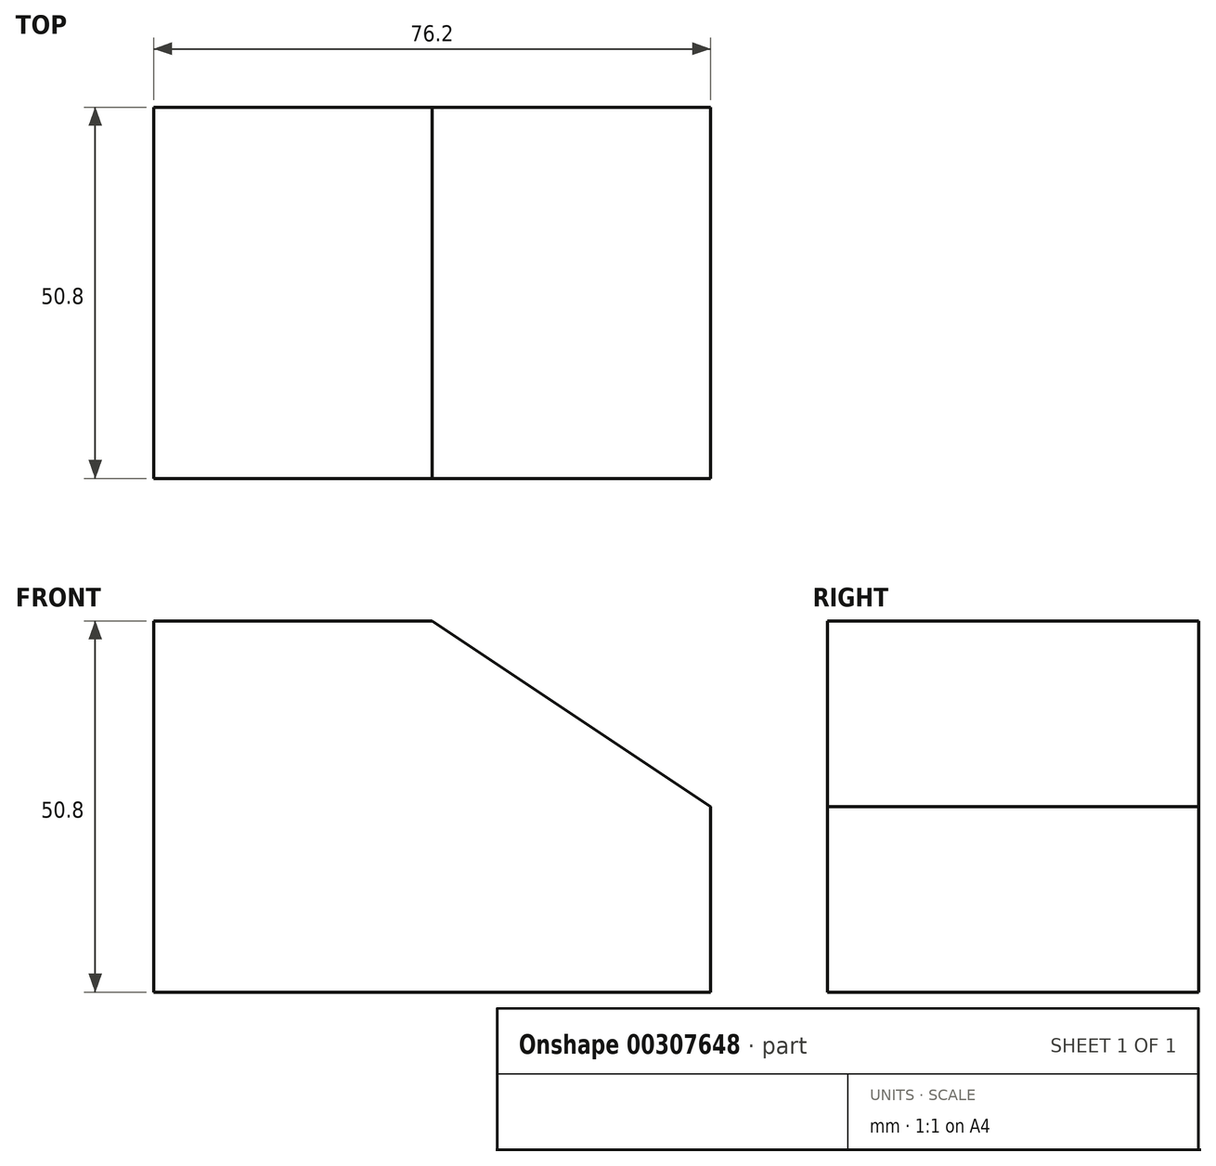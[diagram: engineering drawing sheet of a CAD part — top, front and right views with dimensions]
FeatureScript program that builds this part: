
annotation { "Feature Type Name" : "Feature", "Feature Type Description" : "" }
export const myFeature = defineFeature(function(context is Context, id is Id, definition is map)
    precondition{}
    {
        {
            var Q0;
            Q0=qCreatedBy(makeId("Front.planeOp"),FACE);
            var sketch = newSketch(context, id + "F0", { "sketchPlane" : qUnion([Q0])});
            skLineSegment(sketch, "E0", {"start": v(-58, -18.72) * mm, "end": v(18.2, -18.72) * mm});
            skLineSegment(sketch, "E1", {"start": v(18.2, -18.72) * mm, "end": v(18.2, 6.68) * mm});
            skLineSegment(sketch, "E2", {"start": v(-58, -18.72) * mm, "end": v(-58, 32.08) * mm});
            skLineSegment(sketch, "E3", {"start": v(-58, 32.08) * mm, "end": v(-19.9, 32.08) * mm});
            skLineSegment(sketch, "E4", {"start": v(-19.9, 32.08) * mm, "end": v(18.2, 6.68) * mm});
            skSolve(sketch);
        }
        {
            var Q0;
            Q0 = qSketchRegion(id + "F0", true);
            extrude(context, id + "F1", {"entities" : qUnion([Q0]), "depth" : 50.8 * mm});
        }
    });
